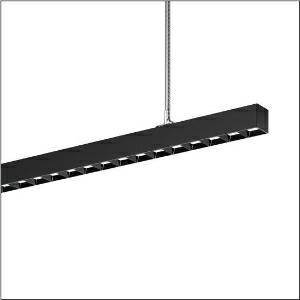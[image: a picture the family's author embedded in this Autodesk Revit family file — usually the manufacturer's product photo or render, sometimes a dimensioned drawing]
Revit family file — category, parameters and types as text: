
# Revit family: silica_r__21_51mx31dc4dbb_76cd
name_source: partatom
category: Lighting Fixtures
units: mm (PartAtom-declared; Revit-internal decimal feet)

## family parameters
Cut with Voids When Loaded = No
Host = Face
Light Source = No
Part Type = Normal
Room Calculation Point = No
Round Connector Dimension = Use Diameter
Shared = No

## types (1)
- --- (1 x LED, 18230 lm, 105.9 W, 4000K)
    Apparent Load = 106 VA
    CIE Flux Codes = 87 99 100 59 100
    Color Rendering = 80
    Color Temperature = 4000K
    Default Elevation = 1800 mm
    Description = Silica® 21, office luminaire, primary light control with darklight reflector, of PMMA, black, CAT 2 (L<= 3000cd/m²), light emission: direct/indirect distribution, primary light characteristic: symmetric, installation type: suspended mounting, LED, rated luminous flux: 18.230lm, luminous efficacy: 172lm/W, light colour: 840, colour temperature: 4000K, with terminal, 3+2-pole, max. 2.5mm², mains connection: 220..240V, AC, 50/60Hz, rated input power: 105.9W, luminaire housing, of aluminium, jet black (RAL 9005), length: 3.004mm, width: 53mm, height: 53mm, protection rating (complete): IP20, insulation class (complete): insulation class I (protective earthing), certification: CE, permissible operating ambient temperature: 0..+35°C, standard: EN 50419, packaging unit: 1 piece
    Height = 53 mm
    Lamp = 1 x LED
    Lamp Light Flux = 18230 lm
    Lamp Power = 105.9 W
    Lamp count = 1
    Length = 3004 mm
    Luminous efficacy = 172 lm/W
    Manufacturer = Siteco
    ModVariant = No
    Model = 51MX31DC4DBB
    Mounting Place = Ceiling
    Mounting Type = Pendant
    Number of Poles = 1
    OnlyDefault = Yes
    Power Factor = 1
    Product Name = Silica® 21
    Product group = office luminaire | ceiling pendant
    ProductGroupID = 905
    Protection Class = Protection class I
    Protection Degree = IP 20
    RLX_Detail_Level = 1
    RlxData = <blob elided: 67281 chars, md5=4cf21395>
    Socket = socket
    Standby Power = 0 W
    System Light Flux = 18230 lm
    System Power = 106 W
    Type Comments = factory setting: luminous flux: 100 % | dim-lin: 254 | 367 mA
    Type Image = l_1251718.jpg
    URL = http://relux.com
    VarID = @adj_030161
    Voltage = 0 V
    Weight = 0.00 kg
    Width = 53 mm

## geometry (parser evidence)
native form markers: Blend x4, Sweep x11
no freeform markers — native parametric forms only
